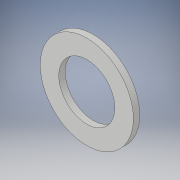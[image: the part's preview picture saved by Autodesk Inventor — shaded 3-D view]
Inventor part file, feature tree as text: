
AUTODESK INVENTOR PART (.ipt)
format: ipt  version: 2018 (Build 220112000, 112)  size: 98,816 bytes
history: native  units: mm
features: extrude x1, sketch x1
ambient origin geometry x8: Origin, YZ Plane, XZ Plane, XY Plane, X Axis, Y Axis, Z Axis, Center Point
bodies: Volumenkörper1 (feature_tree)
feature tree (2):
  extrude  "Extrusion1"  Depth=4.0mm
  sketch  "Skizze1"  dims[d0=35.0mm d1=58.2mm d2=4.0mm d3=0.0mm]
